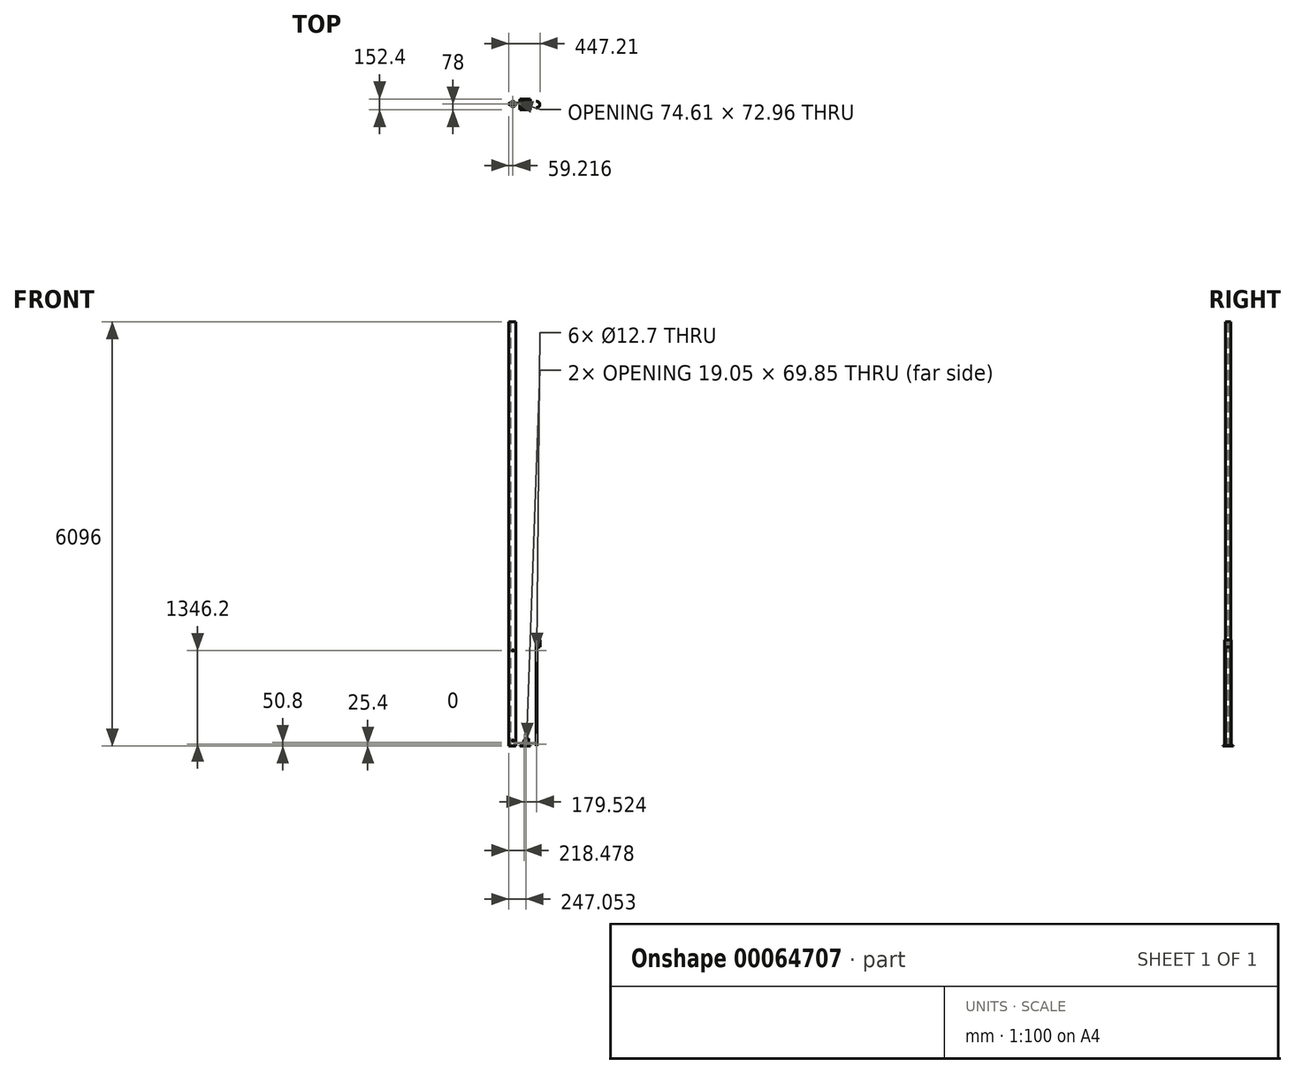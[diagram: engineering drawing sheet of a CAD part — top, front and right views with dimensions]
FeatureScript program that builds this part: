
annotation { "Feature Type Name" : "Feature", "Feature Type Description" : "" }
export const myFeature = defineFeature(function(context is Context, id is Id, definition is map)
    precondition{}
    {
        {
            var Q0;
            Q0=qCreatedBy(makeId("Top.planeOp"),FACE);
            var sketch = newSketch(context, id + "F0", { "sketchPlane" : qUnion([Q0])});
            skArc(sketch, "E0", {"start": v(-20.81, -31.91) * mm, "mid": v(38.1, 0) * mm, "end": v(-20.81, 31.91) * mm});
            skArc(sketch, "E1", {"start": v(-19.95, -30.58) * mm, "mid": v(36.51, 0) * mm, "end": v(-19.95, 30.58) * mm});
            skLineSegment(sketch, "E2", {"start": v(-39.69, 17.7) * mm, "end": v(-39.69, -17.7) * mm});
            skLineSegment(sketch, "E3", {"start": v(-60, 6.35) * mm, "end": v(-60, 3.17) * mm});
            skLineSegment(sketch, "E4", {"start": v(54.56, 0) * mm, "end": v(-73.78, 0) * mm, "construction": true});
            skLineSegment(sketch, "E5", {"start": v(-39.69, 0) * mm, "end": v(-60, 0) * mm});
            skLineSegment(sketch, "E6", {"start": v(-60, 6.35) * mm, "end": v(-20.81, 31.91) * mm});
            skLineSegment(sketch, "E7", {"start": v(-60, -6.35) * mm, "end": v(-20.81, -31.91) * mm});
            skLineSegment(sketch, "E8", {"start": v(-38.1, 18.74) * mm, "end": v(-38.1, -18.74) * mm});
            skLineSegment(sketch, "E9", {"start": v(-58.42, 5.5) * mm, "end": v(-58.42, 3.17) * mm});
            skLineSegment(sketch, "E10", {"start": v(-58.42, 5.5) * mm, "end": v(-39.69, 17.7) * mm});
            skLineSegment(sketch, "E11", {"start": v(-58.42, -5.5) * mm, "end": v(-39.69, -17.7) * mm});
            skLineSegment(sketch, "E12.bottom", {"start": v(-60, 3.17) * mm, "end": v(-58.42, 3.17) * mm});
            skLineSegment(sketch, "E12.top", {"start": v(-60, -3.18) * mm, "end": v(-58.42, -3.18) * mm});
            skLineSegment(sketch, "E12.left", {"start": v(-60, 3.17) * mm, "end": v(-60, -3.18) * mm});
            skPoint(sketch, "E13.orphan", {"position": v(-39.69, -19.05) * mm});
            skLineSegment(sketch, "E14.trimOffspring", {"start": v(-38.1, -18.74) * mm, "end": v(-19.95, -30.58) * mm});
            skLineSegment(sketch, "E15.trimOffspring", {"start": v(-38.1, 18.74) * mm, "end": v(-19.95, 30.58) * mm});
            skPoint(sketch, "E16.orphan", {"position": v(-39.69, 19.05) * mm});
            skPoint(sketch, "E17.orphan", {"position": v(-55.05, 3.17) * mm});
            skPoint(sketch, "E18.orphan", {"position": v(-55.05, -3.18) * mm});
            skLineSegment(sketch, "E19.trimOffspring", {"start": v(-58.42, -3.18) * mm, "end": v(-58.42, -5.5) * mm});
            skLineSegment(sketch, "E20.trimOffspring", {"start": v(-60, -3.18) * mm, "end": v(-60, -6.35) * mm});
            skSolve(sketch);
        }
        {
            var Q0;
            Q0=makeQuery(id+"F0.imprint","IMPRINT",FACE,{"disambiguationData":[TD([[makeQuery(id+"F0.imprint","IMPRINT",EDGE,{"derivedFrom":sQuery(id+"F0.wireOp",EDGE,"E0")}),1.0]])]});
            extrude(context, id + "F1", {"entities" : qUnion([Q0]), "depth" : 6096 * mm});
        }
        {
            var Q0;
            Q0=qCreatedBy(makeId("Front.planeOp"),FACE);
            var sketch = newSketch(context, id + "F2", { "sketchPlane" : qUnion([Q0])});
            skLineSegment(sketch, "E21", {"start": v(0, 0) * mm, "end": v(0, 1371.6) * mm, "construction": true});
            skCircle(sketch, "E22", {"center": v(0, 1371.6) * mm, "radius": 9.53 * mm});
            skCircle(sketch, "E23", {"center": v(0, 76.2) * mm, "radius": 9.53 * mm});
            skSolve(sketch);
        }
        {
            var Q0;
            Q0 = qSketchRegion(id + "F2", true);
            extrude(context, id + "F3", {"entities" : qUnion([Q0]), "operationType" : NewBodyOperationType.ADD, "endBound" : BoundingType.SYMMETRIC, "oppositeDirection" : true, "depth" : 76.2 * mm});
        }
        {
            var Q0;
            Q0=qCreatedBy(makeId("Top.planeOp"),FACE);
            var sketch = newSketch(context, id + "F4", { "sketchPlane" : qUnion([Q0])});
            skLineSegment(sketch, "E24.bottom", {"start": v(94.97, 74.4) * mm, "end": v(247.37, 74.4) * mm});
            skLineSegment(sketch, "E24.top", {"start": v(94.97, -78) * mm, "end": v(247.37, -78) * mm});
            skLineSegment(sketch, "E24.left", {"start": v(94.97, 74.4) * mm, "end": v(94.97, -78) * mm});
            skLineSegment(sketch, "E24.right", {"start": v(247.37, 74.4) * mm, "end": v(247.37, -78) * mm});
            skSolve(sketch);
        }
        {
            var Q0;
            Q0 = qSketchRegion(id + "F4", true);
            extrude(context, id + "F5", {"entities" : qUnion([Q0]), "depth" : 3.17 * mm});
        }
        {
            var Q0;
            Q0=makeQuery(id+"F5.opExtrude","CAP_FACE",FACE,{"disambiguationData":[OSD([sQuery(id+"F4.wireOp",EDGE,"E24.bottom"),sQuery(id+"F4.wireOp",EDGE,"E24.top"),sQuery(id+"F4.wireOp",EDGE,"E24.left"),sQuery(id+"F4.wireOp",EDGE,"E24.right")])],"isStart":false});
            var sketch = newSketch(context, id + "F6", { "sketchPlane" : qUnion([Q0])});
            skLineSegment(sketch, "E25.bottom", {"start": v(120.37, 42.65) * mm, "end": v(221.97, 42.65) * mm});
            skLineSegment(sketch, "E25.top", {"start": v(120.37, 36.3) * mm, "end": v(221.97, 36.3) * mm});
            skLineSegment(sketch, "E25.left", {"start": v(120.37, 42.65) * mm, "end": v(120.37, 36.3) * mm});
            skLineSegment(sketch, "E25.right", {"start": v(221.97, 42.65) * mm, "end": v(221.97, 36.3) * mm});
            skLineSegment(sketch, "E26.bottom", {"start": v(120.37, -39.9) * mm, "end": v(221.97, -39.9) * mm});
            skLineSegment(sketch, "E26.top", {"start": v(120.37, -46.25) * mm, "end": v(221.97, -46.25) * mm});
            skLineSegment(sketch, "E26.left", {"start": v(120.37, -39.9) * mm, "end": v(120.37, -46.25) * mm});
            skLineSegment(sketch, "E26.right", {"start": v(221.97, -39.9) * mm, "end": v(221.97, -46.25) * mm});
            skLineSegment(sketch, "E27", {"start": v(247.37, -1.8) * mm, "end": v(94.97, -1.8) * mm, "construction": true});
            skLineSegment(sketch, "E28", {"start": v(171.17, 74.4) * mm, "end": v(171.17, -78) * mm, "construction": true});
            skSolve(sketch);
        }
        {
            var Q0;
            Q0=makeQuery(id+"F6.imprint","IMPRINT",FACE,{"disambiguationData":[TD([[makeQuery(id+"F6.imprint","IMPRINT",EDGE,{"derivedFrom":sQuery(id+"F6.wireOp",EDGE,"E25.bottom")}),-1.0]])]});
            var Q1;
            Q1=makeQuery(id+"F6.imprint","IMPRINT",FACE,{"disambiguationData":[TD([[makeQuery(id+"F6.imprint","IMPRINT",EDGE,{"derivedFrom":sQuery(id+"F6.wireOp",EDGE,"E26.bottom")}),-1.0]])]});
            extrude(context, id + "F7", {"entities" : qUnion([Q0, Q1]), "operationType" : NewBodyOperationType.ADD, "depth" : 101.6 * mm});
        }
        {
            var Q0;
            Q0=makeQuery(id+"F7.opExtrude","SWEPT_FACE",FACE,{"disambiguationData":[OSD([sQuery(id+"F6.wireOp",EDGE,"E26.top")])]});
            var sketch = newSketch(context, id + "F8", { "sketchPlane" : qUnion([Q0])});
            skLineSegment(sketch, "E29.bottom", {"start": v(183.87, 85.73) * mm, "end": v(190.22, 85.73) * mm});
            skLineSegment(sketch, "E29.top", {"start": v(183.87, 15.87) * mm, "end": v(190.22, 15.87) * mm});
            skLineSegment(sketch, "E29.left", {"start": v(177.52, 79.38) * mm, "end": v(177.52, 22.23) * mm});
            skLineSegment(sketch, "E29.right", {"start": v(196.57, 79.38) * mm, "end": v(196.57, 22.23) * mm});
            skLineSegment(sketch, "E30", {"start": v(120.37, 3.17) * mm, "end": v(171.17, 104.78) * mm});
            skPoint(sketch, "E31.visualSharp", {"position": v(177.52, 85.73) * mm});
            skArc(sketch, "E31.filletArc", {"start": v(183.87, 85.73) * mm, "mid": v(179.38, 83.87) * mm, "end": v(177.52, 79.38) * mm});
            skPoint(sketch, "E32.visualSharp", {"position": v(196.57, 85.73) * mm});
            skArc(sketch, "E32.filletArc", {"start": v(196.57, 79.38) * mm, "mid": v(194.7, 83.87) * mm, "end": v(190.22, 85.72) * mm});
            skPoint(sketch, "E33.visualSharp", {"position": v(177.52, 15.87) * mm});
            skArc(sketch, "E33.filletArc", {"start": v(177.52, 22.23) * mm, "mid": v(179.38, 17.73) * mm, "end": v(183.87, 15.88) * mm});
            skPoint(sketch, "E34.visualSharp", {"position": v(196.57, 15.87) * mm});
            skArc(sketch, "E34.filletArc", {"start": v(190.22, 15.88) * mm, "mid": v(194.7, 17.73) * mm, "end": v(196.57, 22.23) * mm});
            skCircle(sketch, "E35", {"center": v(158.47, 28.58) * mm, "radius": 6.35 * mm});
            skSolve(sketch);
        }
        {
            var Q0;
            Q0 = qSketchRegion(id + "F8", true);
            var Q1;
            {var subQ0=sQuery(id+"F8.wireOp",EDGE,"E30");Q1=makeQuery(id+"F8.imprint","IMPRINT",FACE,{"disambiguationData":[TD([[makeQuery(id+"F8.imprint","IMPRINT",EDGE,{"derivedFrom":subQ0}),1.0]])]});}
            extrude(context, id + "F9", {"entities" : qUnion([Q0, Q1]), "operationType" : NewBodyOperationType.REMOVE, "endBound" : BoundingType.THROUGH_ALL, "oppositeDirection" : true, "depth" : 25.4 * mm});
        }
        {
            var Q0;
            Q0=qCreatedBy(makeId("Top.planeOp"),FACE);
            var sketch = newSketch(context, id + "F10", { "sketchPlane" : qUnion([Q0])});
            skLineSegment(sketch, "E36.bottom", {"start": v(330.05, 37.92) * mm, "end": v(345.22, 37.92) * mm});
            skLineSegment(sketch, "E36.top", {"start": v(330.05, -50.98) * mm, "end": v(345.22, -50.98) * mm});
            skLineSegment(sketch, "E37", {"start": v(288.26, -6.53) * mm, "end": v(397.25, -6.53) * mm, "construction": true});
            skArc(sketch, "E38", {"start": v(360.32, -43.88) * mm, "mid": v(384.03, -6.53) * mm, "end": v(360.32, 30.82) * mm});
            skLineSegment(sketch, "E39.0", {"start": v(330.05, 41.1) * mm, "end": v(345.93, 41.1) * mm});
            skLineSegment(sketch, "E40.0", {"start": v(330.05, -54.15) * mm, "end": v(345.93, -54.15) * mm});
            skLineSegment(sketch, "E41.left", {"start": v(330.05, 41.1) * mm, "end": v(330.05, 37.92) * mm});
            skLineSegment(sketch, "E42", {"start": v(345.93, 41.1) * mm, "end": v(361.67, 33.7) * mm});
            skPoint(sketch, "E43.startSnap0", {"position": v(338, 41.1) * mm});
            skLineSegment(sketch, "E44.MirrorCS", {"start": v(345.93, -54.15) * mm, "end": v(361.67, -46.76) * mm});
            skLineSegment(sketch, "E45.trimOffspring", {"start": v(330.05, -50.98) * mm, "end": v(330.05, -54.15) * mm});
            skLineSegment(sketch, "E46.trimOffspring", {"start": v(345.22, 37.92) * mm, "end": v(360.32, 30.82) * mm});
            skPoint(sketch, "E43.start.orphan", {"position": v(338, 41.32) * mm});
            skPoint(sketch, "E47.orphan", {"position": v(376.05, 26.93) * mm});
            skPoint(sketch, "E48.trimOffspring.end.orphan", {"position": v(387.54, 18.02) * mm});
            skPoint(sketch, "E49.orphan", {"position": v(387.54, -31.08) * mm});
            skPoint(sketch, "E50.orphan", {"position": v(376.05, -40) * mm});
            skLineSegment(sketch, "E51.trimOffspring", {"start": v(345.22, -50.98) * mm, "end": v(360.32, -43.88) * mm});
            skArc(sketch, "E52.trimOffspring", {"start": v(361.67, -46.76) * mm, "mid": v(387.2, -6.53) * mm, "end": v(361.67, 33.7) * mm});
            skPoint(sketch, "E53.MirrorCS.start.orphan", {"position": v(338, -54.38) * mm});
            skPoint(sketch, "E54.orphan", {"position": v(288.26, -50.98) * mm});
            skPoint(sketch, "E36.left.start.orphan", {"position": v(288.26, 37.92) * mm});
            skPoint(sketch, "E55.orphan", {"position": v(397.25, 37.92) * mm});
            skPoint(sketch, "E36.right.end.orphan", {"position": v(397.25, -50.98) * mm});
            skSolve(sketch);
        }
        {
            var Q0;
            Q0 = qSketchRegion(id + "F10", true);
            extrude(context, id + "F11", {"entities" : qUnion([Q0]), "depth" : 1524 * mm});
        }
        {
            var Q0;
            Q0=makeQuery(id+"F11.opExtrude","SWEPT_FACE",FACE,{"disambiguationData":[OSD([sQuery(id+"F10.wireOp",EDGE,"E40.0")])]});
            var sketch = newSketch(context, id + "F12", { "sketchPlane" : qUnion([Q0])});
            skLineSegment(sketch, "E56.bottom", {"start": v(345.93, 0) * mm, "end": v(420.94, 0) * mm});
            skLineSegment(sketch, "E56.top", {"start": v(345.93, 1422.4) * mm, "end": v(420.94, 1422.4) * mm});
            skLineSegment(sketch, "E56.left", {"start": v(345.93, 0) * mm, "end": v(345.93, 1422.4) * mm});
            skLineSegment(sketch, "E56.right", {"start": v(420.94, 0) * mm, "end": v(420.94, 1422.4) * mm});
            skSolve(sketch);
        }
        {
            var Q0;
            Q0 = qSketchRegion(id + "F12", true);
            extrude(context, id + "F13", {"entities" : qUnion([Q0]), "operationType" : NewBodyOperationType.REMOVE, "endBound" : BoundingType.THROUGH_ALL, "oppositeDirection" : true, "depth" : 25.4 * mm});
        }
        {
            var Q0;
            Q0=makeQuery(id+"F11.opExtrude","SWEPT_FACE",FACE,{"disambiguationData":[OSD([sQuery(id+"F10.wireOp",EDGE,"E40.0")])]});
            var sketch = newSketch(context, id + "F14", { "sketchPlane" : qUnion([Q0])});
            skCircle(sketch, "E57", {"center": v(338, 1371.6) * mm, "radius": 6.35 * mm});
            skCircle(sketch, "E58", {"center": v(338, 25.4) * mm, "radius": 6.35 * mm});
            skSolve(sketch);
        }
        {
            var Q0;
            Q0 = qSketchRegion(id + "F14", true);
            extrude(context, id + "F15", {"entities" : qUnion([Q0]), "operationType" : NewBodyOperationType.REMOVE, "endBound" : BoundingType.THROUGH_ALL, "oppositeDirection" : true, "depth" : 25.4 * mm});
        }
    });
